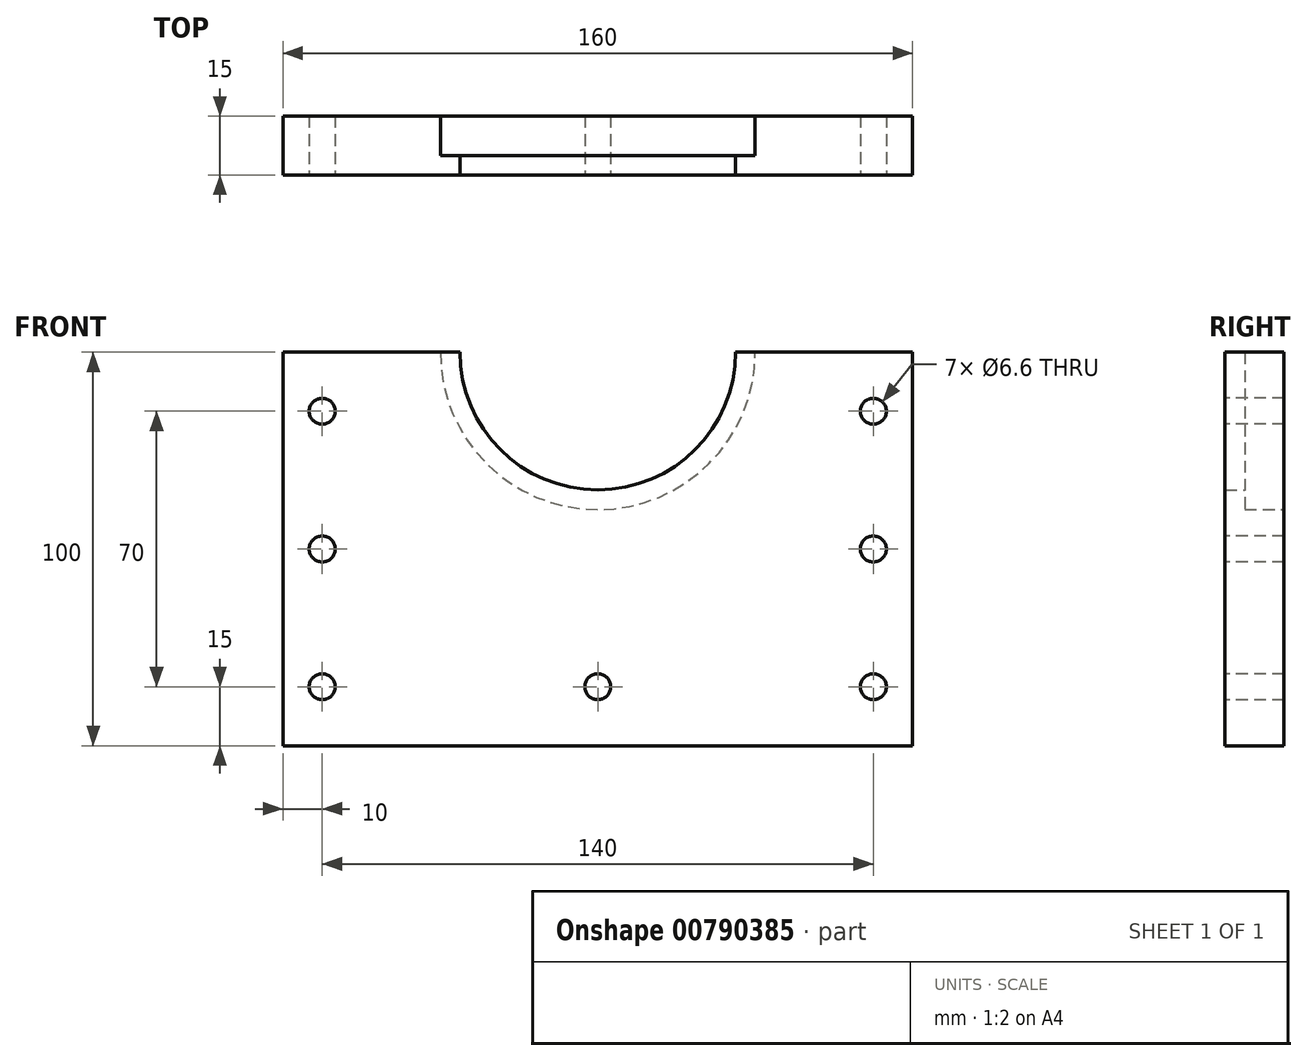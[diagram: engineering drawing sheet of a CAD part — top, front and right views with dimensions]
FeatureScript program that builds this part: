
annotation { "Feature Type Name" : "Feature", "Feature Type Description" : "" }
export const myFeature = defineFeature(function(context is Context, id is Id, definition is map)
    precondition{}
    {
        {
            var Q0;
            Q0=qCreatedBy(makeId("Front.planeOp"),FACE);
            var sketch = newSketch(context, id + "F0", { "sketchPlane" : qUnion([Q0])});
            skArc(sketch, "E0", {"start": v(-40, 40) * mm, "mid": v(0, 0) * mm, "end": v(40, 40) * mm});
            skLineSegment(sketch, "E1.top", {"start": v(80, 40) * mm, "end": v(40, 40) * mm});
            skLineSegment(sketch, "E1.left", {"start": v(80, -60) * mm, "end": v(80, 40) * mm});
            skLineSegment(sketch, "E1.right", {"start": v(-80, -60) * mm, "end": v(-80, 40) * mm});
            skPoint(sketch, "E1.middle", {"position": v(0, 0) * mm});
            skLineSegment(sketch, "E2.trimOffspring", {"start": v(-40, 40) * mm, "end": v(-80, 40) * mm});
            skLineSegment(sketch, "E3", {"start": v(-80, -60) * mm, "end": v(80, -60) * mm});
            skPoint(sketch, "E4", {"position": v(-70, 25) * mm});
            skPoint(sketch, "E5", {"position": v(70, 25) * mm});
            skPoint(sketch, "E6", {"position": v(70, -10) * mm});
            skPoint(sketch, "E7", {"position": v(-70, -10) * mm});
            skPoint(sketch, "E8", {"position": v(-70, -45) * mm});
            skPoint(sketch, "E9", {"position": v(70, -45) * mm});
            skPoint(sketch, "E10", {"position": v(0, -45) * mm});
            skSolve(sketch);
        }
        {
            var Q0;
            Q0=makeQuery(id+"F0.imprint","IMPRINT",FACE,{"disambiguationData":[TD([[makeQuery(id+"F0.imprint","IMPRINT",EDGE,{"derivedFrom":sQuery(id+"F0.wireOp",EDGE,"E0")}),-1.0]])]});
            extrude(context, id + "F1", {"entities" : qUnion([Q0]), "depth" : 10 * mm, "offsetDistance" : 25 * mm});
        }
        {
            var Q0;
            Q0=sQuery(id+"F0.wireOp",VERTEX,"E4");
            var Q1;
            Q1=sQuery(id+"F0.wireOp",VERTEX,"E7");
            var Q2;
            Q2=sQuery(id+"F0.wireOp",VERTEX,"E8");
            var Q3;
            Q3=sQuery(id+"F0.wireOp",VERTEX,"E10");
            var Q4;
            Q4=sQuery(id+"F0.wireOp",VERTEX,"E9");
            var Q5;
            Q5=sQuery(id+"F0.wireOp",VERTEX,"E5");
            var Q6;
            Q6=sQuery(id+"F0.wireOp",VERTEX,"E6");
            var Q7;
            Q7=makeQuery(id+"F1.opExtrude","SWEPT_BODY",BODY,{"disambiguationData":[OSD([sQuery(id+"F0.wireOp",EDGE,"E0"),sQuery(id+"F0.wireOp",EDGE,"E1.top"),sQuery(id+"F0.wireOp",EDGE,"E1.left"),sQuery(id+"F0.wireOp",EDGE,"E1.right"),sQuery(id+"F0.wireOp",EDGE,"E2.trimOffspring"),sQuery(id+"F0.wireOp",EDGE,"E3")])]});
            hole(context, id + "F2", {"style" : HoleStyle.SIMPLE, "endStyle" : HoleEndStyle.BLIND, "oppositeDirection" : true, "standardTappedOrClearance" : lookupTablePath({ "standard" : "ISO", "fit" : "Normal", "size" : "M6", "type" : "Clearance" }), "standardBlindInLast" : lookupTablePath({ "fit" : "Standard", "standard" : "ISO", "size" : "M6", "type" : "Clearance" }), "holeDiameter" : 6.6 * mm, "majorDiameter" : 6 * mm, "holeDepth" : 14.25 * mm, "isTappedThrough" : true, "tappedDepth" : 11.25 * mm, "tapClearance" : 3, "startFromSketch" : true, "locations" : qUnion([Q0, Q1, Q2, Q3, Q4, Q5, Q6]), "scope" : qUnion([Q7])});
        }
        {
            var Q0;
            Q0=makeQuery(id+"F1.opExtrude","CAP_FACE",FACE,{"disambiguationData":[OSD([sQuery(id+"F0.wireOp",EDGE,"E0"),sQuery(id+"F0.wireOp",EDGE,"E1.top"),sQuery(id+"F0.wireOp",EDGE,"E1.left"),sQuery(id+"F0.wireOp",EDGE,"E1.right"),sQuery(id+"F0.wireOp",EDGE,"E2.trimOffspring"),sQuery(id+"F0.wireOp",EDGE,"E3")])],"isStart":false});
            var sketch = newSketch(context, id + "F3", { "sketchPlane" : qUnion([Q0])});
            skArc(sketch, "E11", {"start": v(-35, 40) * mm, "mid": v(0, 5) * mm, "end": v(35, 40) * mm});
            skPoint(sketch, "E11.centerSnap0", {"position": v(0, 0) * mm});
            skLineSegment(sketch, "E12", {"start": v(-40, 40) * mm, "end": v(-35, 40) * mm});
            skLineSegment(sketch, "E13.trimOffspring", {"start": v(35, 40) * mm, "end": v(40, 40) * mm});
            skSolve(sketch);
        }
        {
            var Q0;
            {var subQ5=sQuery(id+"F0.wireOp",EDGE,"E0");Q0=makeQuery(id+"F3.imprint","IMPRINT",FACE,{"disambiguationData":[TD([[makeQuery(id+"F3.imprint","IMPRINT",EDGE,{"derivedFrom":makeQuery(id+"F1.opExtrude","CAP_EDGE",EDGE,{"disambiguationData":[OSD([subQ5])],"isStart":false})}),-1.0]])]});}
            var Q1;
            Q1=makeQuery(id+"F3.imprint","IMPRINT",FACE,{"disambiguationData":[TD([[makeQuery(id+"F3.imprint","IMPRINT",EDGE,{"derivedFrom":sQuery(id+"F3.wireOp",EDGE,"E11")}),-1.0]])]});
            extrude(context, id + "F4", {"entities" : qUnion([Q0, Q1]), "operationType" : NewBodyOperationType.ADD, "depth" : 5 * mm, "offsetDistance" : 25 * mm});
        }
    });
